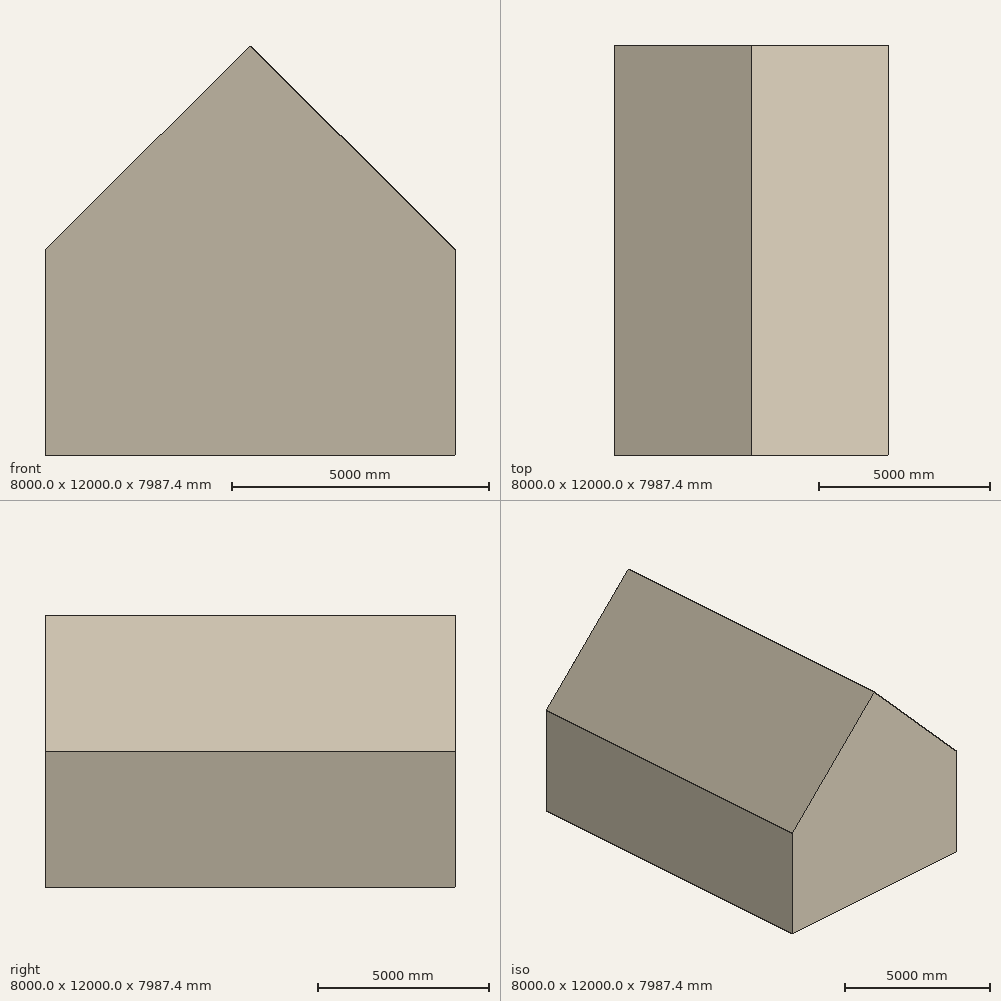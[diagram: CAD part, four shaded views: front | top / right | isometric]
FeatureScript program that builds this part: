
annotation { "Feature Type Name" : "Feature", "Feature Type Description" : "" }
export const myFeature = defineFeature(function(context is Context, id is Id, definition is map)
    precondition{}
    {
        {
            var Q0;
            Q0=qCreatedBy(makeId("Front.planeOp"),FACE);
            var sketch = newSketch(context, id + "F0", { "sketchPlane" : qUnion([Q0])});
            skLineSegment(sketch, "E0", {"start": v(0, 0) * mm, "end": v(8000, 0) * mm});
            skLineSegment(sketch, "E1", {"start": v(0, 0) * mm, "end": v(0, 4000) * mm});
            skLineSegment(sketch, "E2", {"start": v(8000, 0) * mm, "end": v(8000, 4000) * mm});
            skLineSegment(sketch, "E3", {"start": v(0, 4000) * mm, "end": v(0, 8000) * mm});
            skLineSegment(sketch, "E4", {"start": v(0, 4000) * mm, "end": v(3999.98, 7987.44) * mm});
            skLineSegment(sketch, "E5", {"start": v(3999.98, 7987.44) * mm, "end": v(8000, 4000) * mm});
            skSolve(sketch);
        }
        {
            var Q0;
            Q0=makeQuery(id+"F0.imprint","IMPRINT",FACE,{"disambiguationData":[TD([[makeQuery(id+"F0.imprint","IMPRINT",EDGE,{"derivedFrom":sQuery(id+"F0.wireOp",EDGE,"E0")}),1.0]])]});
            extrude(context, id + "F1", {"entities" : qUnion([Q0]), "depth" : 12000 * mm});
        }
    });
